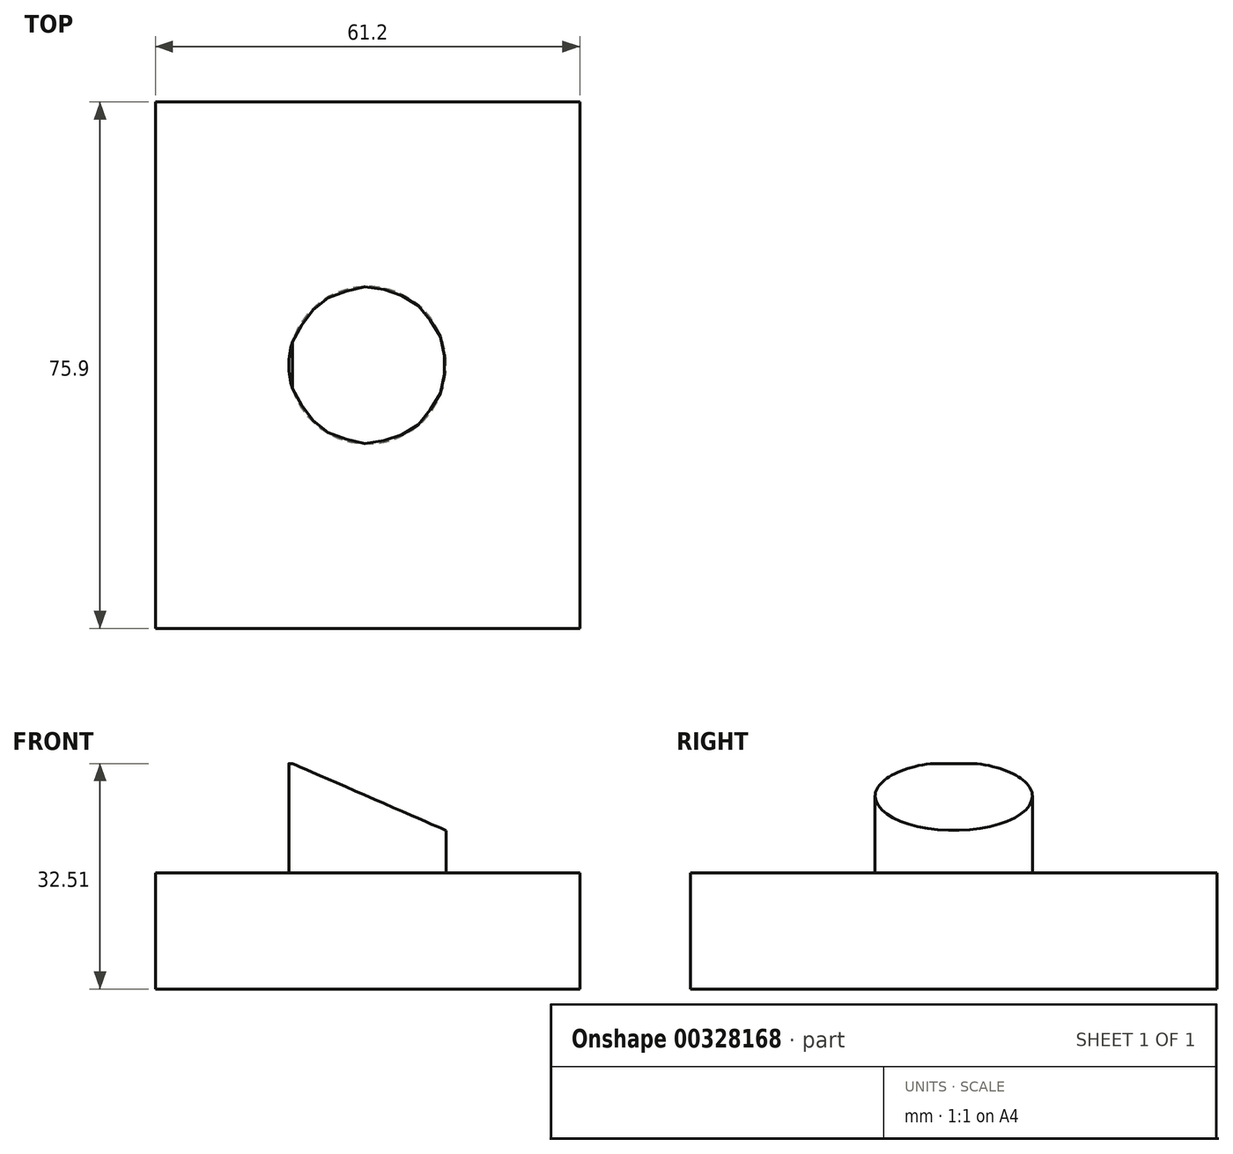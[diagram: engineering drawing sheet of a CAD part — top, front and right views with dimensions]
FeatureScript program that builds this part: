
annotation { "Feature Type Name" : "Feature", "Feature Type Description" : "" }
export const myFeature = defineFeature(function(context is Context, id is Id, definition is map)
    precondition{}
    {
        {
            var Q0;
            Q0=qCreatedBy(makeId("Top.planeOp"),FACE);
            var sketch = newSketch(context, id + "F0", { "sketchPlane" : qUnion([Q0])});
            skLineSegment(sketch, "E0.bottom", {"start": v(-30.6, 37.95) * mm, "end": v(30.6, 37.95) * mm});
            skLineSegment(sketch, "E0.top", {"start": v(-30.6, -37.95) * mm, "end": v(30.6, -37.95) * mm});
            skLineSegment(sketch, "E0.left", {"start": v(-30.6, 37.95) * mm, "end": v(-30.6, -37.95) * mm});
            skLineSegment(sketch, "E0.right", {"start": v(30.6, 37.95) * mm, "end": v(30.6, -37.95) * mm});
            skPoint(sketch, "E0.middle", {"position": v(0, 0) * mm});
            skSolve(sketch);
        }
        {
            var Q0;
            Q0=makeQuery(id+"F0.imprint","IMPRINT",FACE,{"disambiguationData":[TD([[makeQuery(id+"F0.imprint","IMPRINT",EDGE,{"derivedFrom":sQuery(id+"F0.wireOp",EDGE,"E0.bottom")}),-1.0]])]});
            extrude(context, id + "F1", {"entities" : qUnion([Q0]), "depth" : 16.76 * mm});
        }
        {
            var Q0;
            Q0=makeQuery(id+"F1.opExtrude","CAP_FACE",FACE,{"disambiguationData":[OSD([sQuery(id+"F0.wireOp",EDGE,"E0.bottom"),sQuery(id+"F0.wireOp",EDGE,"E0.top"),sQuery(id+"F0.wireOp",EDGE,"E0.left"),sQuery(id+"F0.wireOp",EDGE,"E0.right")])],"isStart":false});
            var sketch = newSketch(context, id + "F2", { "sketchPlane" : qUnion([Q0])});
            skCircle(sketch, "E1", {"center": v(0, 0) * mm, "radius": 11.36 * mm});
            skSolve(sketch);
        }
        {
            var Q0;
            Q0 = qSketchRegion(id + "F2", true);
            extrude(context, id + "F3", {"entities" : qUnion([Q0]), "operationType" : NewBodyOperationType.ADD, "depth" : 15.75 * mm});
        }
        {
            var Q0;
            Q0=qCreatedBy(makeId("Front.planeOp"),FACE);
            var sketch = newSketch(context, id + "F4", { "sketchPlane" : qUnion([Q0])});
            skLineSegment(sketch, "E2", {"start": v(-11.23, 32.68) * mm, "end": v(12.62, 22.28) * mm});
            skLineSegment(sketch, "E3", {"start": v(12.62, 22.28) * mm, "end": v(12.62, 32.68) * mm});
            skLineSegment(sketch, "E4", {"start": v(12.62, 32.68) * mm, "end": v(-11.23, 32.68) * mm});
            skSolve(sketch);
        }
        {
            var Q0;
            Q0 = qSketchRegion(id + "F4", true);
            extrude(context, id + "F5", {"entities" : qUnion([Q0]), "operationType" : NewBodyOperationType.REMOVE, "oppositeDirection" : true, "depth" : 25.4 * mm, "hasSecondDirection" : true, "secondDirectionOppositeDirection" : false, "secondDirectionDepth" : 25.4 * mm});
        }
    });
